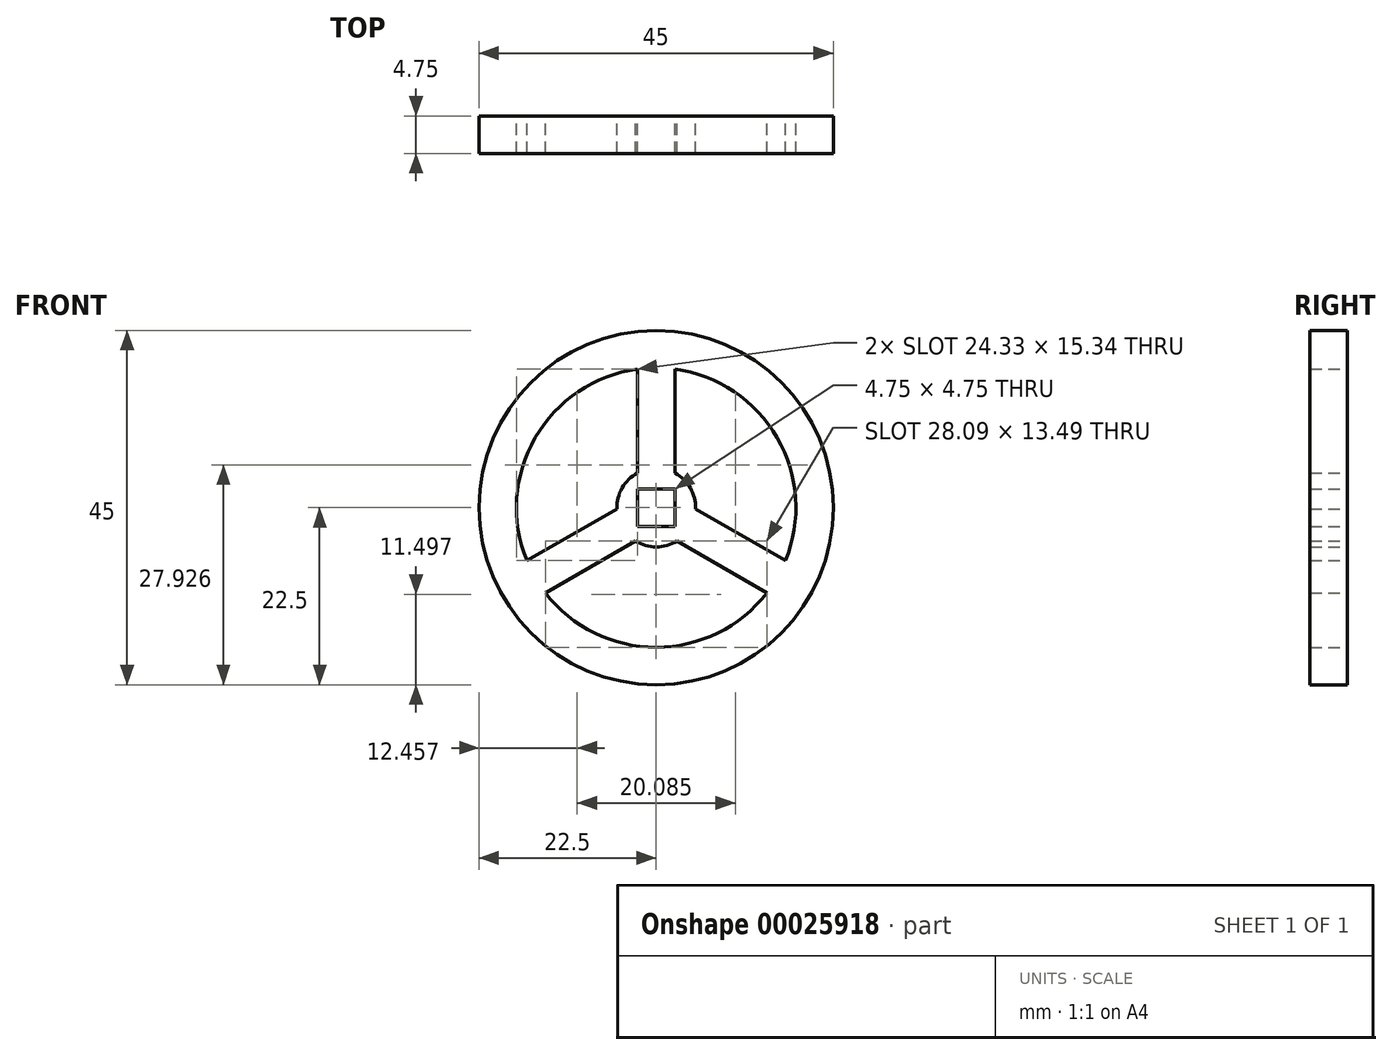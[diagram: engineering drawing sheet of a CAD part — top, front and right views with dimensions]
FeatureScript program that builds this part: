
annotation { "Feature Type Name" : "Feature", "Feature Type Description" : "" }
export const myFeature = defineFeature(function(context is Context, id is Id, definition is map)
    precondition{}
    {
        {
            var Q0;
            Q0=qCreatedBy(makeId("Front.planeOp"),FACE);
            var sketch = newSketch(context, id + "F0", { "sketchPlane" : qUnion([Q0])});
            skCircle(sketch, "E0", {"center": v(0, 0) * mm, "radius": 22.5 * mm});
            skArc(sketch, "E1", {"start": v(-14.05, -10.85) * mm, "mid": v(0, -17.75) * mm, "end": v(14.05, -10.85) * mm});
            skLineSegment(sketch, "E2.rect.bottom", {"start": v(-2.38, 2.38) * mm, "end": v(2.38, 2.38) * mm});
            skLineSegment(sketch, "E2.rect.top", {"start": v(-2.38, -2.38) * mm, "end": v(2.38, -2.38) * mm});
            skLineSegment(sketch, "E2.rect.left", {"start": v(-2.38, 2.38) * mm, "end": v(-2.38, -2.38) * mm});
            skLineSegment(sketch, "E2.rect.right", {"start": v(2.38, 2.38) * mm, "end": v(2.38, -2.38) * mm});
            skArc(sketch, "E3", {"start": v(-2.62, -4.26) * mm, "mid": v(0, -5) * mm, "end": v(2.62, -4.26) * mm});
            skLineSegment(sketch, "E4", {"start": v(-2.38, 4.4) * mm, "end": v(-2.38, 17.6) * mm});
            skLineSegment(sketch, "E5", {"start": v(2.38, 4.4) * mm, "end": v(2.38, 17.6) * mm});
            skLineSegment(sketch, "E6", {"start": v(0, 0) * mm, "end": v(-19.49, -11.25) * mm, "construction": true});
            skLineSegment(sketch, "E7", {"start": v(0, 0) * mm, "end": v(19.49, -11.25) * mm, "construction": true});
            skLineSegment(sketch, "E8", {"start": v(-5, -0.14) * mm, "end": v(-16.42, -6.74) * mm});
            skLineSegment(sketch, "E9", {"start": v(-14.05, -10.85) * mm, "end": v(-2.62, -4.26) * mm});
            skLineSegment(sketch, "E10", {"start": v(5, -0.14) * mm, "end": v(16.42, -6.74) * mm});
            skLineSegment(sketch, "E11", {"start": v(2.62, -4.26) * mm, "end": v(14.05, -10.85) * mm});
            skArc(sketch, "E12.trimOffspring", {"start": v(5, -0.14) * mm, "mid": v(4.33, 2.5) * mm, "end": v(2.37, 4.4) * mm});
            skArc(sketch, "E13.trimOffspring", {"start": v(-2.38, 4.4) * mm, "mid": v(-4.33, 2.5) * mm, "end": v(-5, -0.14) * mm});
            skArc(sketch, "E14.trimOffspring", {"start": v(16.42, -6.74) * mm, "mid": v(15.37, 8.88) * mm, "end": v(2.38, 17.6) * mm});
            skArc(sketch, "E15.trimOffspring", {"start": v(-2.38, 17.6) * mm, "mid": v(-15.37, 8.87) * mm, "end": v(-16.42, -6.74) * mm});
            skSolve(sketch);
        }
        {
            var Q0;
            Q0=makeQuery(id+"F0.imprint","IMPRINT",FACE,{"disambiguationData":[TD([[makeQuery(id+"F0.imprint","IMPRINT",EDGE,{"derivedFrom":sQuery(id+"F0.wireOp",EDGE,"E0")}),1.0]])]});
            extrude(context, id + "F1", {"entities" : qUnion([Q0]), "depth" : 4.75 * mm});
        }
    });
